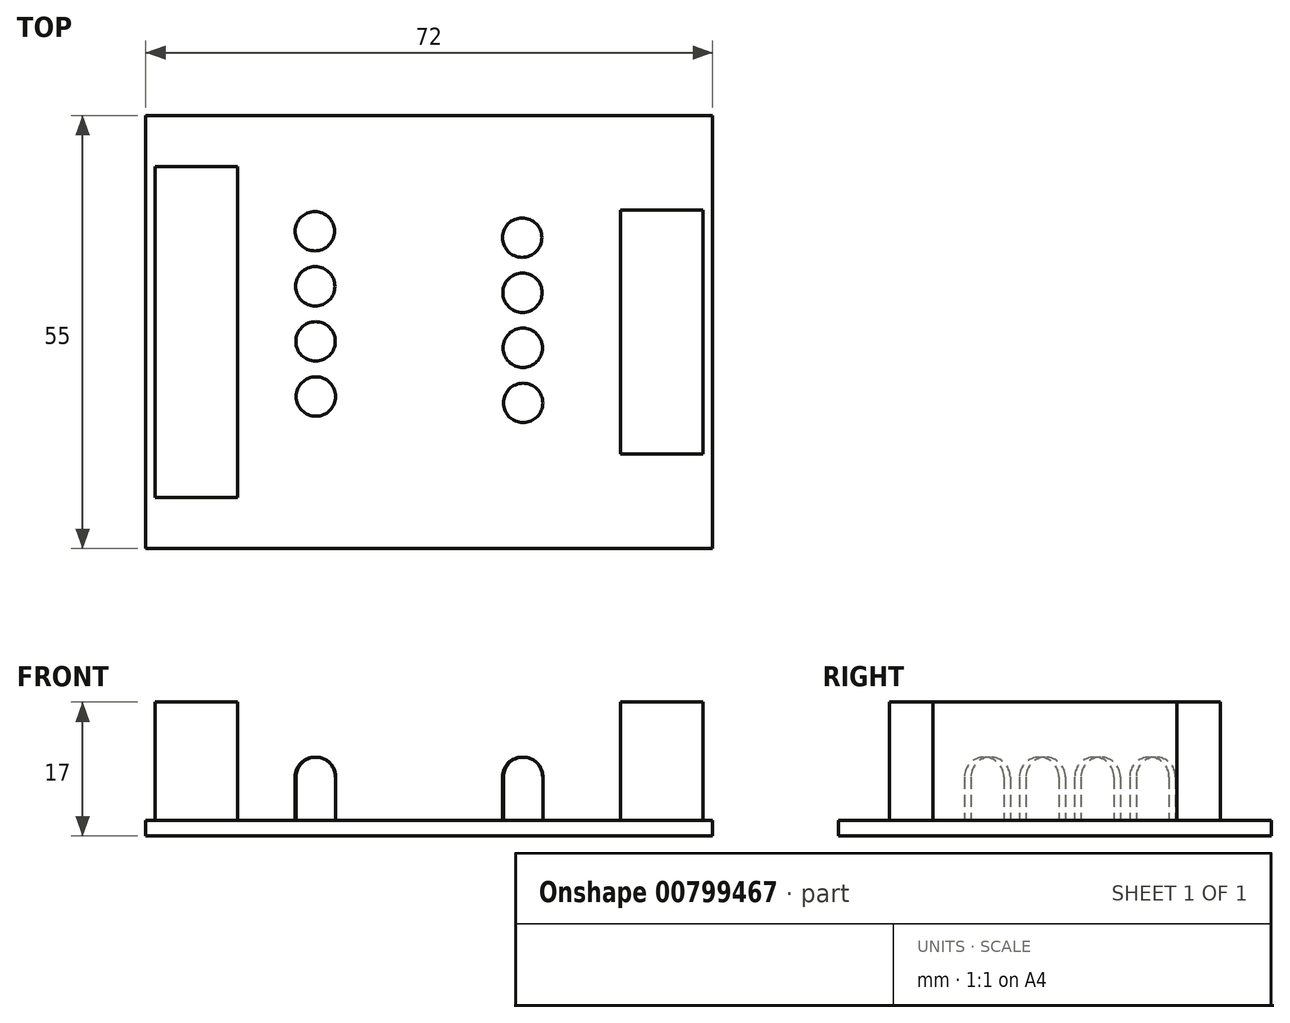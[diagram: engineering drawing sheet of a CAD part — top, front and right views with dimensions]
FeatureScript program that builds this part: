
annotation { "Feature Type Name" : "Feature", "Feature Type Description" : "" }
export const myFeature = defineFeature(function(context is Context, id is Id, definition is map)
    precondition{}
    {
        {
            var Q0;
            Q0=qCreatedBy(makeId("Top.planeOp"),FACE);
            var sketch = newSketch(context, id + "F0", { "sketchPlane" : qUnion([Q0])});
            skLineSegment(sketch, "E0.bottom", {"start": v(0, 0) * mm, "end": v(72, 0) * mm});
            skLineSegment(sketch, "E0.top", {"start": v(0, 55) * mm, "end": v(72, 55) * mm});
            skLineSegment(sketch, "E0.left", {"start": v(0, 0) * mm, "end": v(0, 55) * mm});
            skLineSegment(sketch, "E0.right", {"start": v(72, 0) * mm, "end": v(72, 55) * mm});
            skLineSegment(sketch, "E1.bottom", {"start": v(60.3, 43) * mm, "end": v(70.8, 43) * mm});
            skLineSegment(sketch, "E1.top", {"start": v(60.3, 12) * mm, "end": v(70.8, 12) * mm});
            skLineSegment(sketch, "E1.left", {"start": v(60.3, 43) * mm, "end": v(60.3, 12) * mm});
            skLineSegment(sketch, "E1.right", {"start": v(70.8, 43) * mm, "end": v(70.8, 12) * mm});
            skLineSegment(sketch, "E2.bottom", {"start": v(1.2, 48.5) * mm, "end": v(11.7, 48.5) * mm});
            skLineSegment(sketch, "E2.top", {"start": v(1.2, 6.5) * mm, "end": v(11.7, 6.5) * mm});
            skLineSegment(sketch, "E2.left", {"start": v(1.2, 48.5) * mm, "end": v(1.2, 6.5) * mm});
            skLineSegment(sketch, "E2.right", {"start": v(11.7, 48.5) * mm, "end": v(11.7, 6.5) * mm});
            skCircle(sketch, "E3", {"center": v(21.5, 40.32) * mm, "radius": 2.5 * mm});
            skCircle(sketch, "E4.1.0.0", {"center": v(21.53, 33.32) * mm, "radius": 2.5 * mm});
            skCircle(sketch, "E4.2.0.0", {"center": v(21.58, 26.32) * mm, "radius": 2.5 * mm});
            skCircle(sketch, "E4.3.0.0", {"center": v(21.62, 19.32) * mm, "radius": 2.5 * mm});
            skLineSegment(sketch, "E4.direction1", {"start": v(21.5, 40.32) * mm, "end": v(21.53, 33.32) * mm, "construction": true});
            skCircle(sketch, "E5", {"center": v(47.82, 39.5) * mm, "radius": 2.5 * mm});
            skCircle(sketch, "E6.1.0.0", {"center": v(47.86, 32.5) * mm, "radius": 2.5 * mm});
            skCircle(sketch, "E6.2.0.0", {"center": v(47.9, 25.5) * mm, "radius": 2.5 * mm});
            skCircle(sketch, "E6.3.0.0", {"center": v(47.94, 18.5) * mm, "radius": 2.5 * mm});
            skLineSegment(sketch, "E6.direction1", {"start": v(47.82, 39.5) * mm, "end": v(47.86, 32.5) * mm, "construction": true});
            skSolve(sketch);
        }
        {
            var Q0;
            Q0=makeQuery(id+"F0.imprint","IMPRINT",FACE,{"disambiguationData":[TD([[makeQuery(id+"F0.imprint","IMPRINT",EDGE,{"derivedFrom":sQuery(id+"F0.wireOp",EDGE,"E0.bottom")}),1.0]])]});
            extrude(context, id + "F1", {"entities" : qUnion([Q0]), "depth" : 2 * mm, "offsetDistance" : 25 * mm});
        }
        {
            var Q0;
            Q0=makeQuery(id+"F0.imprint","IMPRINT",FACE,{"disambiguationData":[TD([[makeQuery(id+"F0.imprint","IMPRINT",EDGE,{"derivedFrom":sQuery(id+"F0.wireOp",EDGE,"E1.bottom")}),-1.0]])]});
            var Q1;
            Q1=makeQuery(id+"F0.imprint","IMPRINT",FACE,{"disambiguationData":[TD([[makeQuery(id+"F0.imprint","IMPRINT",EDGE,{"derivedFrom":sQuery(id+"F0.wireOp",EDGE,"E2.bottom")}),-1.0]])]});
            extrude(context, id + "F2", {"entities" : qUnion([Q0, Q1]), "operationType" : NewBodyOperationType.ADD, "depth" : 17 * mm, "offsetDistance" : 25 * mm});
        }
        {
            var Q0;
            Q0=makeQuery(id+"F0.imprint","IMPRINT",FACE,{"disambiguationData":[TD([[makeQuery(id+"F0.imprint","IMPRINT",EDGE,{"derivedFrom":sQuery(id+"F0.wireOp",EDGE,"E3")}),1.0]])]});
            var Q1;
            Q1=makeQuery(id+"F0.imprint","IMPRINT",FACE,{"disambiguationData":[TD([[makeQuery(id+"F0.imprint","IMPRINT",EDGE,{"derivedFrom":sQuery(id+"F0.wireOp",EDGE,"E4.1.0.0")}),1.0]])]});
            var Q2;
            Q2=makeQuery(id+"F0.imprint","IMPRINT",FACE,{"disambiguationData":[TD([[makeQuery(id+"F0.imprint","IMPRINT",EDGE,{"derivedFrom":sQuery(id+"F0.wireOp",EDGE,"E4.2.0.0")}),1.0]])]});
            var Q3;
            Q3=makeQuery(id+"F0.imprint","IMPRINT",FACE,{"disambiguationData":[TD([[makeQuery(id+"F0.imprint","IMPRINT",EDGE,{"derivedFrom":sQuery(id+"F0.wireOp",EDGE,"E4.3.0.0")}),1.0]])]});
            var Q4;
            Q4=makeQuery(id+"F0.imprint","IMPRINT",FACE,{"disambiguationData":[TD([[makeQuery(id+"F0.imprint","IMPRINT",EDGE,{"derivedFrom":sQuery(id+"F0.wireOp",EDGE,"E5")}),1.0]])]});
            var Q5;
            Q5=makeQuery(id+"F0.imprint","IMPRINT",FACE,{"disambiguationData":[TD([[makeQuery(id+"F0.imprint","IMPRINT",EDGE,{"derivedFrom":sQuery(id+"F0.wireOp",EDGE,"E6.1.0.0")}),1.0]])]});
            var Q6;
            Q6=makeQuery(id+"F0.imprint","IMPRINT",FACE,{"disambiguationData":[TD([[makeQuery(id+"F0.imprint","IMPRINT",EDGE,{"derivedFrom":sQuery(id+"F0.wireOp",EDGE,"E6.2.0.0")}),1.0]])]});
            var Q7;
            Q7=makeQuery(id+"F0.imprint","IMPRINT",FACE,{"disambiguationData":[TD([[makeQuery(id+"F0.imprint","IMPRINT",EDGE,{"derivedFrom":sQuery(id+"F0.wireOp",EDGE,"E6.3.0.0")}),1.0]])]});
            extrude(context, id + "F3", {"entities" : qUnion([Q0, Q1, Q2, Q3, Q4, Q5, Q6, Q7]), "operationType" : NewBodyOperationType.ADD, "depth" : 10 * mm, "offsetDistance" : 25 * mm});
        }
        {
            var Q0;
            Q0=makeQuery(id+"F3.opExtrude","CAP_EDGE",EDGE,{"disambiguationData":[OSD([sQuery(id+"F0.wireOp",EDGE,"E3")])],"isStart":false});
            var Q1;
            Q1=makeQuery(id+"F3.opExtrude","CAP_EDGE",EDGE,{"disambiguationData":[OSD([sQuery(id+"F0.wireOp",EDGE,"E4.1.0.0")])],"isStart":false});
            var Q2;
            Q2=makeQuery(id+"F3.opExtrude","CAP_EDGE",EDGE,{"disambiguationData":[OSD([sQuery(id+"F0.wireOp",EDGE,"E4.2.0.0")])],"isStart":false});
            var Q3;
            Q3=makeQuery(id+"F3.opExtrude","CAP_EDGE",EDGE,{"disambiguationData":[OSD([sQuery(id+"F0.wireOp",EDGE,"E4.3.0.0")])],"isStart":false});
            var Q4;
            Q4=makeQuery(id+"F3.opExtrude","CAP_EDGE",EDGE,{"disambiguationData":[OSD([sQuery(id+"F0.wireOp",EDGE,"E5")])],"isStart":false});
            var Q5;
            Q5=makeQuery(id+"F3.opExtrude","CAP_EDGE",EDGE,{"disambiguationData":[OSD([sQuery(id+"F0.wireOp",EDGE,"E6.1.0.0")])],"isStart":false});
            var Q6;
            Q6=makeQuery(id+"F3.opExtrude","CAP_EDGE",EDGE,{"disambiguationData":[OSD([sQuery(id+"F0.wireOp",EDGE,"E6.2.0.0")])],"isStart":false});
            var Q7;
            Q7=makeQuery(id+"F3.opExtrude","CAP_EDGE",EDGE,{"disambiguationData":[OSD([sQuery(id+"F0.wireOp",EDGE,"E6.3.0.0")])],"isStart":false});
            fillet(context, id + "F4", {"entities" : qUnion([Q0, Q1, Q2, Q3, Q4, Q5, Q6, Q7]), "radius" : 2.5 * mm, "tangentPropagation" : true, "allowEdgeOverflow" : false});
        }
    });
